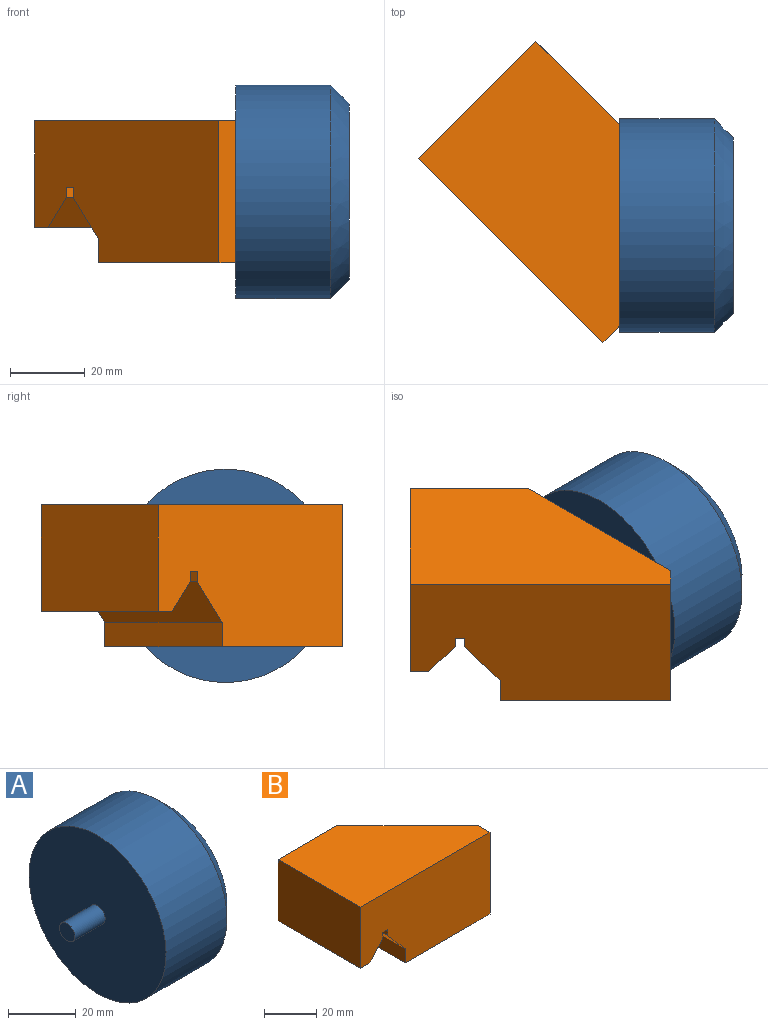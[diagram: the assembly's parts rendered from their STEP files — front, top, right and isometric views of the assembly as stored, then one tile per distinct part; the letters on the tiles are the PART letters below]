
ASSEMBLY  parts=2 mates=1
PART A: 8 faces, bbox 43.2x57.2x57.2 mm
  f0: cone r=28.57mm half-angle=45deg, axis (-1,0,0), area 1175.2mm2, adj f1,f7
  f1: cylinder r=28.57mm len=57.15mm, axis (1,0,0), area 4560.4mm2, adj f0,f2
  f2: plane 57.15x57.15mm, normal (-1,0,0), area 2533.5mm2, adj f1,f3
  f3: cylinder r=3.17mm len=12.7mm, axis (1,0,0), area 253.4mm2, adj f2,f4
  f4: plane 6.35x6.35mm, normal (-1,0,0), area 31.7mm2, adj f3
  f5: plane 41.91x41.91mm, normal (1,0,0), area 1379.5mm2, adj f6
  f6: cylinder r=20.96mm len=41.91mm, axis (1,0,0), area 3177.1mm2, adj f5,f7
  f7: plane 46.99x46.99mm, normal (1,0,0), area 354.7mm2, adj f0,f6
PART B: 16 faces, bbox 69.9x44.5x38.1 mm
  f0: plane 45.72x44.45mm, normal (0,0,-1), area 1306.4mm2, adj f2,f4,f5,f12,f13
  f1: plane 69.85x44.45mm, normal (0,0,1), area 2379mm2, adj f2,f5,f6,f12,f13
  f2: plane 38.1x31.75mm, normal (0,1,0), area 899.8mm2, adj f0,f1,f3,f4,f6,f7,f8,f9
  f3: plane 44.45x10.99mm, normal (-0.76,0,-0.65), area 646.5mm2, adj f2,f4,f11,f12
  f4: plane 44.45x6.59mm, normal (-1,0,0), area 293.1mm2, adj f0,f2,f3,f12
  f5: plane 38.1x6.35mm, normal (1,0,0), area 241.9mm2, adj f0,f1,f12,f13
  f6: plane 44.45x28.58mm, normal (-1,0,0), area 1270.2mm2, adj f1,f2,f7,f12
  f7: plane 44.45x5.08mm, normal (0,0,-1), area 225.8mm2, adj f2,f6,f8,f12
  f8: plane 44.45x8.06mm, normal (0.76,0,-0.65), area 474.1mm2, adj f2,f7,f9,f12
  f9: plane 44.45x2.74mm, normal (1,0,0), area 121.6mm2, adj f2,f8,f10,f12
  f10: plane 44.45x2.54mm, normal (0,0,-1), area 112.9mm2, adj f2,f9,f11,f12
  f11: plane 44.45x2.74mm, normal (-1,0,0), area 121.6mm2, adj f2,f3,f10,f12
  f12: plane 69.85x38.1mm, normal (0,-1,0), area 2351.5mm2, adj f0,f1,f3,f4,f5,f6,f7,f8
  f13: plane 38.1x38.1mm, normal (0.71,0.71,0), area 2021.2mm2, adj f0,f1,f2,f5,f14
  f14: cylinder r=3.17mm len=13.47mm, axis (0.71,0.71,0), area 253.4mm2, adj f13,f15
  f15: plane 6.35x4.49mm, normal (0.71,0.71,0), area 31.7mm2, adj f14
PLACE A t=(49.84,41.88,-68.01)mm
PLACE B rot(axis=(0,0,-1),45deg) t=(40.09,91.27,-87.06)mm
MATE revolute B.f14 <-> A.f0  axis (1,0,0) through (62.54,41.88,-68.01)mm
